# Revit family: BuzziChip
name_source: partatom
category: Lighting Fixtures
units: mm (PartAtom-declared; Revit-internal decimal feet)

## family parameters
Always vertical = Yes
Cut with Voids When Loaded = No
Host = Ceiling
Light Source = No
OmniClass Number = 23.80.70.11
OmniClass Title = Luminaries for Internal Lighting
Part Type = Normal
Room Calculation Point = No
Round Connector Dimension = Use Diameter
Shared = No

## types (6) — shared parameters
Small Lights = Yes

## per-type parameters (varying)
| type | Cable Spacing | Fixture Type | Large Lights | Length | Light Spacing | Medium Lights |
| Small - Globe | 1' - 6 29/32" | BuzziChip - Globe Light | No | 2' - 3 9/16" | 1' - 5 23/32" | No |
| Medium - Globe | 2' - 5 17/32" | BuzziChip - Globe Light | No | 4' - 7 1/8" | 1' - 2 3/4" | Yes |
| Large - Globe | 4' - 11 1/16" | BuzziChip - Globe Light | Yes | 7' - 4 11/16" | 1' - 5 23/32" | Yes |
| Small - Spot | 1' - 6 29/32" | BuzziChip - Spot Light | No | 2' - 3 9/16" | 1' - 5 23/32" | No |
| Medium - Spot | 2' - 5 17/32" | BuzziChip - Spot Light | No | 4' - 7 1/8" | 1' - 2 3/4" | Yes |
| Large - Spot | 4' - 11 1/16" | BuzziChip - Spot Light | Yes | 7' - 4 11/16" | 1' - 5 23/32" | Yes |

## geometry (parser evidence)
native form markers: Sweep x14
no freeform markers — native parametric forms only
